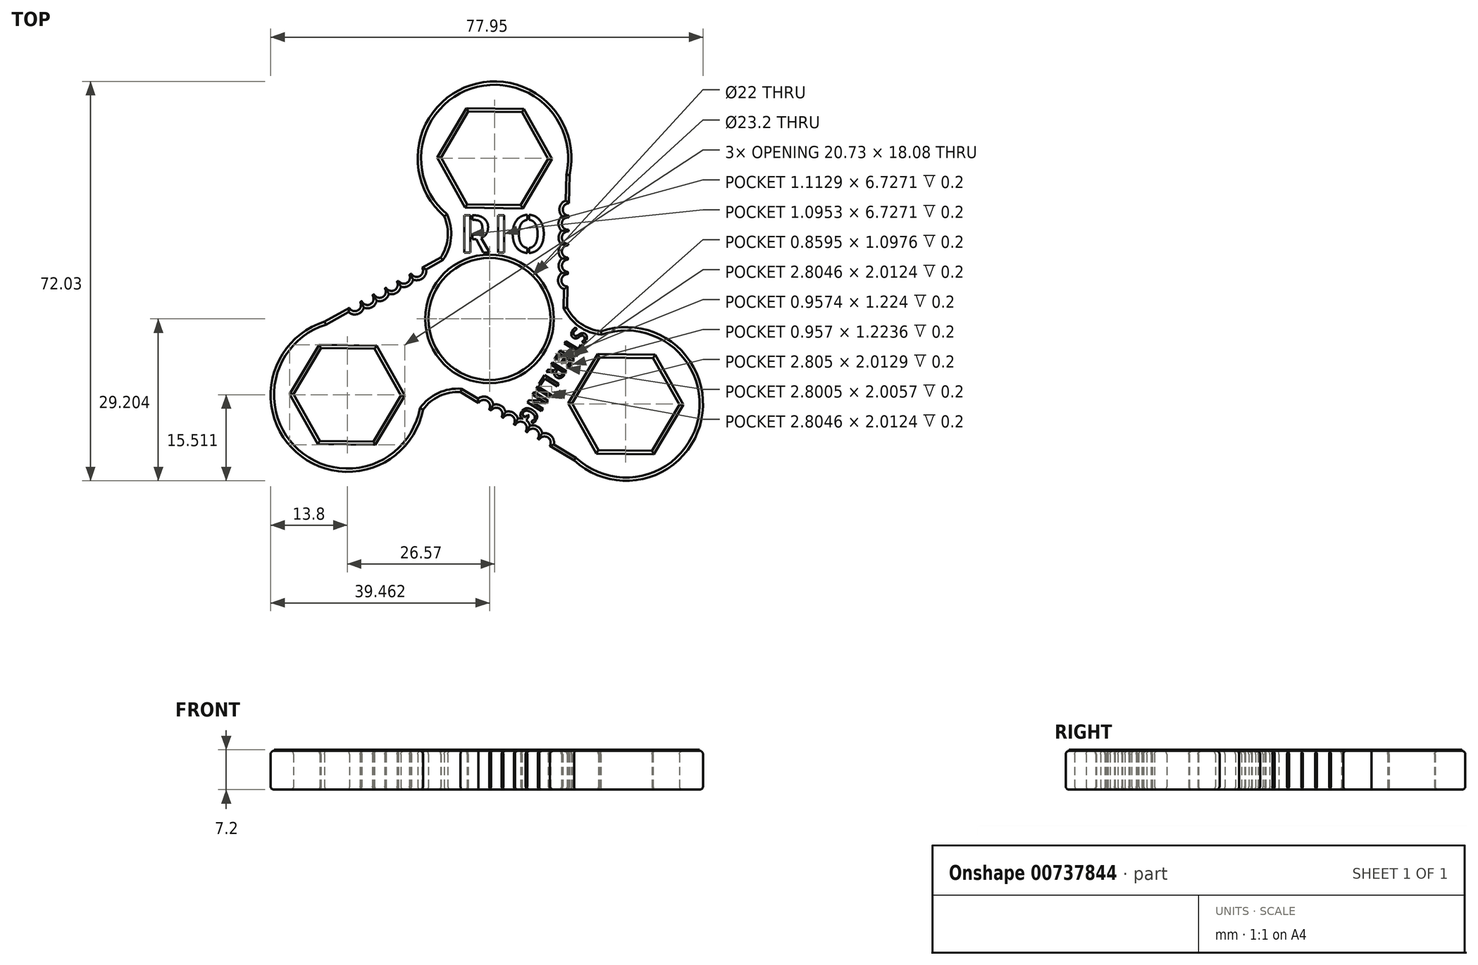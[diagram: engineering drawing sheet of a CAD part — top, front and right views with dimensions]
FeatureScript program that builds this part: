
annotation { "Feature Type Name" : "Feature", "Feature Type Description" : "" }
export const myFeature = defineFeature(function(context is Context, id is Id, definition is map)
    precondition{}
    {
        {
            var Q0;
            Q0=qCreatedBy(makeId("Top.planeOp"),FACE);
            var sketch = newSketch(context, id + "F0", { "sketchPlane" : qUnion([Q0])});
            skCircle(sketch, "E0", {"center": v(0, 0) * mm, "radius": 11 * mm});
            skArc(sketch, "E1", {"start": v(14.5, 25.96) * mm, "mid": v(-3.36, 42.17) * mm, "end": v(-8.1, 18.52) * mm});
            skArc(sketch, "E2", {"start": v(-8.76, 11.09) * mm, "mid": v(-7.48, 14.72) * mm, "end": v(-8.1, 18.52) * mm});
            skLineSegment(sketch, "E3", {"start": v(14.5, 25.96) * mm, "end": v(14.04, 2.08) * mm});
            skCircle(sketch, "E4", {"center": v(14.38, 19.75) * mm, "radius": 1.12 * mm});
            skCircle(sketch, "E5", {"center": v(14.2, 17.22) * mm, "radius": 1.12 * mm});
            skCircle(sketch, "E6", {"center": v(14.22, 14.68) * mm, "radius": 1.12 * mm});
            skCircle(sketch, "E7", {"center": v(14.23, 12.19) * mm, "radius": 1.12 * mm});
            skCircle(sketch, "E8", {"center": v(14.24, 9.62) * mm, "radius": 1.12 * mm});
            skCircle(sketch, "E9", {"center": v(14.14, 6.98) * mm, "radius": 1.12 * mm});
            skArc(sketch, "E10.1.0", {"start": v(-29.67, -0.46) * mm, "mid": v(-34.77, -24.03) * mm, "end": v(-11.93, -16.32) * mm});
            skCircle(sketch, "E10.1.1", {"center": v(0.06, -0.04) * mm, "radius": 11 * mm});
            skLineSegment(sketch, "E10.1.3", {"start": v(-29.67, -0.46) * mm, "end": v(-8.76, 11.09) * mm});
            skArc(sketch, "E10.1.5", {"start": v(-5.16, -13.17) * mm, "mid": v(-8.95, -13.87) * mm, "end": v(-11.93, -16.32) * mm});
            skCircle(sketch, "E10.1.6", {"center": v(-15.39, 7.49) * mm, "radius": 1.12 * mm});
            skCircle(sketch, "E10.1.7", {"center": v(-24.23, 2.54) * mm, "radius": 1.12 * mm});
            skCircle(sketch, "E10.1.8", {"center": v(-21.96, 3.66) * mm, "radius": 1.12 * mm});
            skCircle(sketch, "E10.1.9", {"center": v(-13.05, 8.71) * mm, "radius": 1.12 * mm});
            skCircle(sketch, "E10.1.10", {"center": v(-17.6, 6.2) * mm, "radius": 1.12 * mm});
            skCircle(sketch, "E10.1.11", {"center": v(-19.76, 4.94) * mm, "radius": 1.12 * mm});
            skArc(sketch, "E10.2.0", {"start": v(15.3, -25.5) * mm, "mid": v(38.26, -18.13) * mm, "end": v(20.16, -2.2) * mm});
            skCircle(sketch, "E10.2.1", {"center": v(0.06, 0.03) * mm, "radius": 11 * mm});
            skLineSegment(sketch, "E10.2.3", {"start": v(15.3, -25.5) * mm, "end": v(-5.16, -13.17) * mm});
            skArc(sketch, "E10.2.5", {"start": v(14.04, 2.08) * mm, "mid": v(16.55, -0.85) * mm, "end": v(20.16, -2.2) * mm});
            skCircle(sketch, "E10.2.6", {"center": v(1.27, -17.1) * mm, "radius": 1.12 * mm});
            skCircle(sketch, "E10.2.7", {"center": v(9.98, -22.3) * mm, "radius": 1.12 * mm});
            skCircle(sketch, "E10.2.8", {"center": v(7.87, -20.88) * mm, "radius": 1.12 * mm});
            skCircle(sketch, "E10.2.9", {"center": v(-0.96, -15.7) * mm, "radius": 1.12 * mm});
            skCircle(sketch, "E10.2.10", {"center": v(3.5, -18.38) * mm, "radius": 1.12 * mm});
            skCircle(sketch, "E10.2.11", {"center": v(5.66, -19.62) * mm, "radius": 1.12 * mm});
            skPoint(sketch, "E10.center", {"position": v(0.04, 0) * mm});
            skPoint(sketch, "E11.orphan", {"position": v(14, 0) * mm});
            skPoint(sketch, "E12.orphan", {"position": v(13.84, 2.53) * mm});
            skPoint(sketch, "E13.orphan", {"position": v(-4.67, -13.21) * mm});
            skPoint(sketch, "E14.orphan", {"position": v(-6.94, -12.1) * mm});
            skPoint(sketch, "E15.orphan", {"position": v(-6.94, 12.09) * mm});
            skPoint(sketch, "E16.orphan", {"position": v(-9.05, 10.69) * mm});
            skCircle(sketch, "E17.cCircle", {"center": v(0.97, 29) * mm, "radius": 9.67 * mm, "construction": true});
            skLineSegment(sketch, "E17.0", {"start": v(-3.97, 20.69) * mm, "end": v(-8.7, 29.12) * mm});
            skLineSegment(sketch, "E17.1", {"start": v(-8.7, 29.12) * mm, "end": v(-3.76, 37.43) * mm});
            skLineSegment(sketch, "E17.2", {"start": v(-3.76, 37.43) * mm, "end": v(5.91, 37.31) * mm});
            skLineSegment(sketch, "E17.3", {"start": v(5.91, 37.31) * mm, "end": v(10.64, 28.88) * mm});
            skLineSegment(sketch, "E17.4", {"start": v(10.64, 28.88) * mm, "end": v(5.7, 20.56) * mm});
            skLineSegment(sketch, "E17.5", {"start": v(5.7, 20.56) * mm, "end": v(-3.97, 20.69) * mm});
            skCircle(sketch, "E18.1.0", {"center": v(-25.6, -13.66) * mm, "radius": 9.67 * mm, "construction": true});
            skLineSegment(sketch, "E18.1.1", {"start": v(-20.66, -5.35) * mm, "end": v(-15.93, -13.78) * mm});
            skLineSegment(sketch, "E18.1.2", {"start": v(-15.93, -13.78) * mm, "end": v(-20.87, -22.1) * mm});
            skLineSegment(sketch, "E18.1.3", {"start": v(-20.87, -22.1) * mm, "end": v(-30.54, -21.97) * mm});
            skLineSegment(sketch, "E18.1.4", {"start": v(-30.54, -21.97) * mm, "end": v(-35.27, -13.54) * mm});
            skLineSegment(sketch, "E18.1.5", {"start": v(-35.27, -13.54) * mm, "end": v(-30.33, -5.22) * mm});
            skLineSegment(sketch, "E18.1.6", {"start": v(-30.33, -5.22) * mm, "end": v(-20.66, -5.35) * mm});
            skCircle(sketch, "E18.2.0", {"center": v(24.63, -15.34) * mm, "radius": 9.67 * mm, "construction": true});
            skLineSegment(sketch, "E18.2.1", {"start": v(14.96, -15.22) * mm, "end": v(19.9, -6.9) * mm});
            skLineSegment(sketch, "E18.2.2", {"start": v(19.9, -6.9) * mm, "end": v(29.57, -7.03) * mm});
            skLineSegment(sketch, "E18.2.3", {"start": v(29.57, -7.03) * mm, "end": v(34.3, -15.46) * mm});
            skLineSegment(sketch, "E18.2.4", {"start": v(34.3, -15.46) * mm, "end": v(29.36, -23.78) * mm});
            skLineSegment(sketch, "E18.2.5", {"start": v(29.36, -23.78) * mm, "end": v(19.69, -23.65) * mm});
            skLineSegment(sketch, "E18.2.6", {"start": v(19.69, -23.65) * mm, "end": v(14.96, -15.22) * mm});
            skSolve(sketch);
        }
        {
            var Q0;
            {var subQ13=sQuery(id+"F0.wireOp",EDGE,"E10.2.2");var subQ15=makeQuery(id+"F0.imprint","IMPRINT",VERTEX,{"disambiguationData":[OD(0.0)],"derivedFrom":subQ13});Q0=makeQuery(id+"F0.imprint","IMPRINT",FACE,{"disambiguationData":[TD([[makeQuery(id+"F0.imprint","IMPRINT",EDGE,{"disambiguationData":[TD([[subQ15,-1.0]])],"derivedFrom":subQ13}),-1.0]])]});}
            var Q1;
            {var subQ20=sQuery(id+"F0.wireOp",EDGE,"E10.2.2");var subQ23=makeQuery(id+"F0.imprint","IMPRINT",VERTEX,{"disambiguationData":[OD(1.0)],"derivedFrom":subQ20});Q1=makeQuery(id+"F0.imprint","IMPRINT",FACE,{"disambiguationData":[TD([[makeQuery(id+"F0.imprint","IMPRINT",EDGE,{"disambiguationData":[TD([[subQ23,1.0]])],"derivedFrom":subQ20}),-1.0]])]});}
            var Q2;
            Q2=makeQuery(id+"F0.imprint","IMPRINT",FACE,{"disambiguationData":[TD([[makeQuery(id+"F0.imprint","IMPRINT",EDGE,{"derivedFrom":sQuery(id+"F0.wireOp",EDGE,"5nIq9WOL-Nd7C-9ICE-MlP4-sHmHCP0NrJly")}),-1.0]])]});
            var Q3;
            Q3=makeQuery(id+"F0.imprint","IMPRINT",FACE,{"disambiguationData":[TD([[makeQuery(id+"F0.imprint","IMPRINT",EDGE,{"derivedFrom":sQuery(id+"F0.wireOp",EDGE,"E10.2.1")}),-1.0]])]});
            var Q4;
            {var subQ24=sQuery(id+"F0.wireOp",EDGE,"E10.2.2");var subQ27=makeQuery(id+"F0.imprint","IMPRINT",VERTEX,{"disambiguationData":[OD(2.0)],"derivedFrom":subQ24});Q4=makeQuery(id+"F0.imprint","IMPRINT",FACE,{"disambiguationData":[TD([[makeQuery(id+"F0.imprint","IMPRINT",EDGE,{"disambiguationData":[TD([[subQ27,1.0]])],"derivedFrom":subQ24}),-1.0]])]});}
            var Q5;
            {var subQ0=sQuery(id+"F0.wireOp",EDGE,"E10.2.2");var subQ1=sQuery(id+"F0.wireOp",EDGE,"E3");var subQ2=makeQuery(id+"F0.imprint","INTERSECT",VERTEX,{"derivedFrom":[subQ1,subQ0]});Q5=makeQuery(id+"F0.imprint","IMPRINT",FACE,{"disambiguationData":[TD([[makeQuery(id+"F0.imprint","IMPRINT",EDGE,{"disambiguationData":[TD([[subQ2,1.0]])],"derivedFrom":subQ1}),-1.0]])]});}
            var Q6;
            {var subQ0=sQuery(id+"F0.wireOp",EDGE,"E10.2.3");var subQ1=sQuery(id+"F0.wireOp",EDGE,"E10.2.0");var subQ2=makeQuery(id+"F0.imprint","INTERSECT",VERTEX,{"disambiguationData":[OD(0.0)],"derivedFrom":[subQ1,subQ0]});Q6=makeQuery(id+"F0.imprint","IMPRINT",FACE,{"disambiguationData":[TD([[makeQuery(id+"F0.imprint","IMPRINT",EDGE,{"disambiguationData":[TD([[subQ2,1.0]])],"derivedFrom":subQ1}),1.0]])]});}
            var Q7;
            {var subQ0=sQuery(id+"F0.wireOp",EDGE,"E3");var subQ1=sQuery(id+"F0.wireOp",EDGE,"E1");var subQ2=makeQuery(id+"F0.imprint","INTERSECT",VERTEX,{"disambiguationData":[OD(0.0)],"derivedFrom":[subQ1,subQ0]});Q7=makeQuery(id+"F0.imprint","IMPRINT",FACE,{"disambiguationData":[TD([[makeQuery(id+"F0.imprint","IMPRINT",EDGE,{"disambiguationData":[TD([[subQ2,1.0]])],"derivedFrom":subQ1}),1.0]])]});}
            var Q8;
            {var subQ0=sQuery(id+"F0.wireOp",EDGE,"E10.1.3");var subQ1=sQuery(id+"F0.wireOp",EDGE,"E10.1.0");var subQ2=makeQuery(id+"F0.imprint","INTERSECT",VERTEX,{"disambiguationData":[OD(0.0)],"derivedFrom":[subQ1,subQ0]});Q8=makeQuery(id+"F0.imprint","IMPRINT",FACE,{"disambiguationData":[TD([[makeQuery(id+"F0.imprint","IMPRINT",EDGE,{"disambiguationData":[TD([[subQ2,1.0]])],"derivedFrom":subQ1}),1.0]])]});}
            var Q9;
            {var subQ0=sQuery(id+"F0.wireOp",EDGE,"E10.2.2");var subQ1=sQuery(id+"F0.wireOp",EDGE,"E2");var subQ2=makeQuery(id+"F0.imprint","INTERSECT",VERTEX,{"derivedFrom":[subQ1,subQ0]});Q9=makeQuery(id+"F0.imprint","IMPRINT",FACE,{"disambiguationData":[TD([[makeQuery(id+"F0.imprint","IMPRINT",EDGE,{"disambiguationData":[TD([[subQ2,-1.0]])],"derivedFrom":subQ1}),-1.0]])]});}
            var Q10;
            {var subQ0=sQuery(id+"F0.wireOp",EDGE,"E10.2.2");var subQ1=sQuery(id+"F0.wireOp",EDGE,"E10.1.5");var subQ2=makeQuery(id+"F0.imprint","INTERSECT",VERTEX,{"derivedFrom":[subQ1,subQ0]});Q10=makeQuery(id+"F0.imprint","IMPRINT",FACE,{"disambiguationData":[TD([[makeQuery(id+"F0.imprint","IMPRINT",EDGE,{"disambiguationData":[TD([[subQ2,-1.0]])],"derivedFrom":subQ1}),-1.0]])]});}
            var Q11;
            Q11=makeQuery(id+"F0.imprint","IMPRINT",FACE,{"disambiguationData":[TD([[makeQuery(id+"F0.imprint","IMPRINT",EDGE,{"derivedFrom":sQuery(id+"F0.wireOp",EDGE,"E10.1.4")}),-1.0]])]});
            var Q12;
            Q12=makeQuery(id+"F0.imprint","IMPRINT",FACE,{"disambiguationData":[TD([[makeQuery(id+"F0.imprint","IMPRINT",EDGE,{"derivedFrom":sQuery(id+"F0.wireOp",EDGE,"E10.2.4")}),-1.0]])]});
            var Q13;
            {var subQ0=sQuery(id+"F0.wireOp",EDGE,"E10.2.2");var subQ1=sQuery(id+"F0.wireOp",EDGE,"E1");var subQ2=makeQuery(id+"F0.imprint","INTERSECT",VERTEX,{"disambiguationData":[OD(0.0)],"derivedFrom":[subQ1,subQ0]});Q13=makeQuery(id+"F0.imprint","IMPRINT",FACE,{"disambiguationData":[TD([[makeQuery(id+"F0.imprint","IMPRINT",EDGE,{"disambiguationData":[TD([[subQ2,-1.0]])],"derivedFrom":subQ1}),1.0]])]});}
            var Q14;
            {var subQ0=sQuery(id+"F0.wireOp",EDGE,"E10.2.2");var subQ1=sQuery(id+"F0.wireOp",EDGE,"E10.2.0");var subQ2=makeQuery(id+"F0.imprint","INTERSECT",VERTEX,{"disambiguationData":[OD(0.0)],"derivedFrom":[subQ1,subQ0]});Q14=makeQuery(id+"F0.imprint","IMPRINT",FACE,{"disambiguationData":[TD([[makeQuery(id+"F0.imprint","IMPRINT",EDGE,{"disambiguationData":[TD([[subQ2,-1.0]])],"derivedFrom":subQ1}),1.0]])]});}
            var Q15;
            {var subQ0=sQuery(id+"F0.wireOp",EDGE,"E10.2.2");var subQ1=sQuery(id+"F0.wireOp",EDGE,"E10.1.0");var subQ2=makeQuery(id+"F0.imprint","INTERSECT",VERTEX,{"disambiguationData":[OD(0.0)],"derivedFrom":[subQ1,subQ0]});Q15=makeQuery(id+"F0.imprint","IMPRINT",FACE,{"disambiguationData":[TD([[makeQuery(id+"F0.imprint","IMPRINT",EDGE,{"disambiguationData":[TD([[subQ2,-1.0]])],"derivedFrom":subQ1}),1.0]])]});}
            extrude(context, id + "F1", {"entities" : qUnion([Q0, Q1, Q2, Q3, Q4, Q5, Q6, Q7, Q8, Q9, Q10, Q11, Q12, Q13, Q14, Q15]), "depth" : 7 * mm, "offsetDistance" : 25 * mm});
        }
        {
            var Q0;
            Q0=makeQuery(id+"F1.opExtrude","CAP_EDGE",EDGE,{"disambiguationData":[OSD([sQuery(id+"F0.wireOp",EDGE,"E10.1.5")])],"isStart":false});
            var Q1;
            {var subQ0=sQuery(id+"F0.wireOp",EDGE,"E10.2.3");Q1=makeQuery(id+"F1.opExtrude","CAP_EDGE",EDGE,{"disambiguationData":[OSD([subQ0]),TDD([makeQuery(id+"F0.imprint","IMPRINT",EDGE,{"disambiguationData":[TD([[makeQuery(id+"F0.imprint","INTERSECT",VERTEX,{"derivedFrom":[sQuery(id+"F0.wireOp",EDGE,"E10.1.5"),subQ0]}),1.0]])],"derivedFrom":subQ0})])],"isStart":false});}
            var Q2;
            Q2=makeQuery(id+"F1.opExtrude","CAP_EDGE",EDGE,{"disambiguationData":[OSD([sQuery(id+"F0.wireOp",EDGE,"E10.1.0")])],"isStart":false});
            var Q3;
            Q3=makeQuery(id+"F1.opExtrude","CAP_EDGE",EDGE,{"disambiguationData":[OSD([sQuery(id+"F0.wireOp",EDGE,"E10.1.0")])],"isStart":true});
            var Q4;
            {var subQ0=sQuery(id+"F0.wireOp",EDGE,"E10.1.3");Q4=makeQuery(id+"F1.opExtrude","CAP_EDGE",EDGE,{"disambiguationData":[OSD([subQ0]),TDD([makeQuery(id+"F0.imprint","IMPRINT",EDGE,{"disambiguationData":[TD([[makeQuery(id+"F0.imprint","INTERSECT",VERTEX,{"disambiguationData":[OD(1.0)],"derivedFrom":[sQuery(id+"F0.wireOp",EDGE,"E10.1.0"),subQ0]}),-1.0]])],"derivedFrom":subQ0})])],"isStart":true});}
            var Q5;
            {var subQ0=sQuery(id+"F0.wireOp",EDGE,"E10.1.3");Q5=makeQuery(id+"F1.opExtrude","CAP_EDGE",EDGE,{"disambiguationData":[OSD([subQ0]),TDD([makeQuery(id+"F0.imprint","IMPRINT",EDGE,{"disambiguationData":[TD([[makeQuery(id+"F0.imprint","INTERSECT",VERTEX,{"disambiguationData":[OD(1.0)],"derivedFrom":[sQuery(id+"F0.wireOp",EDGE,"E10.1.0"),subQ0]}),-1.0]])],"derivedFrom":subQ0})])],"isStart":false});}
            var Q6;
            Q6=makeQuery(id+"F1.opExtrude","CAP_EDGE",EDGE,{"disambiguationData":[OSD([sQuery(id+"F0.wireOp",EDGE,"E10.1.5")])],"isStart":true});
            var Q7;
            {var subQ0=sQuery(id+"F0.wireOp",EDGE,"E10.2.3");Q7=makeQuery(id+"F1.opExtrude","CAP_EDGE",EDGE,{"disambiguationData":[OSD([subQ0]),TDD([makeQuery(id+"F0.imprint","IMPRINT",EDGE,{"disambiguationData":[TD([[makeQuery(id+"F0.imprint","INTERSECT",VERTEX,{"derivedFrom":[sQuery(id+"F0.wireOp",EDGE,"E10.1.5"),subQ0]}),1.0]])],"derivedFrom":subQ0})])],"isStart":true});}
            var Q8;
            Q8=makeQuery(id+"F1.opExtrude","CAP_EDGE",EDGE,{"disambiguationData":[OSD([sQuery(id+"F0.wireOp",EDGE,"E10.1.4")])],"isStart":false});
            var Q9;
            Q9=makeQuery(id+"F1.opExtrude","CAP_EDGE",EDGE,{"disambiguationData":[OSD([sQuery(id+"F0.wireOp",EDGE,"E10.1.4")])],"isStart":true});
            var Q10;
            Q10=makeQuery(id+"F1.opExtrude","CAP_EDGE",EDGE,{"disambiguationData":[OSD([sQuery(id+"F0.wireOp",EDGE,"E10.2.1")])],"isStart":true});
            var Q11;
            Q11=makeQuery(id+"F1.opExtrude","CAP_EDGE",EDGE,{"disambiguationData":[OSD([sQuery(id+"F0.wireOp",EDGE,"E10.2.1")])],"isStart":false});
            var Q12;
            {var subQ0=sQuery(id+"F0.wireOp",EDGE,"E10.1.3");Q12=makeQuery(id+"F1.opExtrude","CAP_EDGE",EDGE,{"disambiguationData":[OSD([subQ0]),TDD([makeQuery(id+"F0.imprint","IMPRINT",EDGE,{"disambiguationData":[TD([[makeQuery(id+"F0.imprint","INTERSECT",VERTEX,{"derivedFrom":[sQuery(id+"F0.wireOp",EDGE,"E2"),subQ0]}),1.0]])],"derivedFrom":subQ0})])],"isStart":false});}
            var Q13;
            Q13=makeQuery(id+"F1.opExtrude","CAP_EDGE",EDGE,{"disambiguationData":[OSD([sQuery(id+"F0.wireOp",EDGE,"E2")])],"isStart":false});
            var Q14;
            Q14=makeQuery(id+"F1.opExtrude","CAP_EDGE",EDGE,{"disambiguationData":[OSD([sQuery(id+"F0.wireOp",EDGE,"E1")])],"isStart":false});
            var Q15;
            Q15=makeQuery(id+"F1.opExtrude","CAP_EDGE",EDGE,{"disambiguationData":[OSD([sQuery(id+"F0.wireOp",EDGE,"5nIq9WOL-Nd7C-9ICE-MlP4-sHmHCP0NrJly")])],"isStart":false});
            var Q16;
            Q16=makeQuery(id+"F1.opExtrude","CAP_EDGE",EDGE,{"disambiguationData":[OSD([sQuery(id+"F0.wireOp",EDGE,"5nIq9WOL-Nd7C-9ICE-MlP4-sHmHCP0NrJly")])],"isStart":true});
            var Q17;
            Q17=makeQuery(id+"F1.opExtrude","CAP_EDGE",EDGE,{"disambiguationData":[OSD([sQuery(id+"F0.wireOp",EDGE,"E1")])],"isStart":true});
            var Q18;
            Q18=makeQuery(id+"F1.opExtrude","CAP_EDGE",EDGE,{"disambiguationData":[OSD([sQuery(id+"F0.wireOp",EDGE,"E2")])],"isStart":true});
            var Q19;
            {var subQ0=sQuery(id+"F0.wireOp",EDGE,"E10.1.3");Q19=makeQuery(id+"F1.opExtrude","CAP_EDGE",EDGE,{"disambiguationData":[OSD([subQ0]),TDD([makeQuery(id+"F0.imprint","IMPRINT",EDGE,{"disambiguationData":[TD([[makeQuery(id+"F0.imprint","INTERSECT",VERTEX,{"derivedFrom":[sQuery(id+"F0.wireOp",EDGE,"E2"),subQ0]}),1.0]])],"derivedFrom":subQ0})])],"isStart":true});}
            var Q20;
            Q20=makeQuery(id+"F1.opExtrude","CAP_EDGE",EDGE,{"disambiguationData":[OSD([sQuery(id+"F0.wireOp",EDGE,"E10.2.5")])],"isStart":false});
            var Q21;
            {var subQ0=sQuery(id+"F0.wireOp",EDGE,"E3");Q21=makeQuery(id+"F1.opExtrude","CAP_EDGE",EDGE,{"disambiguationData":[OSD([subQ0]),TDD([makeQuery(id+"F0.imprint","IMPRINT",EDGE,{"disambiguationData":[TD([[makeQuery(id+"F0.imprint","INTERSECT",VERTEX,{"disambiguationData":[OD(1.0)],"derivedFrom":[subQ0,sQuery(id+"F0.wireOp",EDGE,"E9")]}),-1.0]])],"derivedFrom":subQ0})])],"isStart":false});}
            var Q22;
            Q22=makeQuery(id+"F1.opExtrude","CAP_EDGE",EDGE,{"disambiguationData":[OSD([sQuery(id+"F0.wireOp",EDGE,"E10.2.0")])],"isStart":false});
            var Q23;
            Q23=makeQuery(id+"F1.opExtrude","CAP_EDGE",EDGE,{"disambiguationData":[OSD([sQuery(id+"F0.wireOp",EDGE,"E10.2.4")])],"isStart":false});
            var Q24;
            Q24=makeQuery(id+"F1.opExtrude","CAP_EDGE",EDGE,{"disambiguationData":[OSD([sQuery(id+"F0.wireOp",EDGE,"E10.2.4")])],"isStart":true});
            var Q25;
            Q25=makeQuery(id+"F1.opExtrude","CAP_EDGE",EDGE,{"disambiguationData":[OSD([sQuery(id+"F0.wireOp",EDGE,"E10.2.5")])],"isStart":true});
            var Q26;
            Q26=makeQuery(id+"F1.opExtrude","CAP_EDGE",EDGE,{"disambiguationData":[OSD([sQuery(id+"F0.wireOp",EDGE,"E10.2.0")])],"isStart":true});
            var Q27;
            Q27=makeQuery(id+"F1.opExtrude","CAP_EDGE",EDGE,{"disambiguationData":[OSD([sQuery(id+"F0.wireOp",EDGE,"E10.1.7")])],"isStart":false});
            var Q28;
            Q28=makeQuery(id+"F1.opExtrude","CAP_FACE",FACE,{"disambiguationData":[OSD([sQuery(id+"F0.wireOp",EDGE,"5nIq9WOL-Nd7C-9ICE-MlP4-sHmHCP0NrJly"),sQuery(id+"F0.wireOp",EDGE,"E1"),sQuery(id+"F0.wireOp",EDGE,"E2"),sQuery(id+"F0.wireOp",EDGE,"E3"),sQuery(id+"F0.wireOp",EDGE,"E4"),sQuery(id+"F0.wireOp",EDGE,"E5"),sQuery(id+"F0.wireOp",EDGE,"E6"),sQuery(id+"F0.wireOp",EDGE,"E7"),sQuery(id+"F0.wireOp",EDGE,"E8"),sQuery(id+"F0.wireOp",EDGE,"E9"),sQuery(id+"F0.wireOp",EDGE,"E10.1.0"),sQuery(id+"F0.wireOp",EDGE,"E10.1.3"),sQuery(id+"F0.wireOp",EDGE,"E10.1.4"),sQuery(id+"F0.wireOp",EDGE,"E10.1.5"),sQuery(id+"F0.wireOp",EDGE,"E10.1.6"),sQuery(id+"F0.wireOp",EDGE,"E10.1.7"),sQuery(id+"F0.wireOp",EDGE,"E10.1.8"),sQuery(id+"F0.wireOp",EDGE,"E10.1.9"),sQuery(id+"F0.wireOp",EDGE,"E10.1.10"),sQuery(id+"F0.wireOp",EDGE,"E10.1.11"),sQuery(id+"F0.wireOp",EDGE,"E10.2.0"),sQuery(id+"F0.wireOp",EDGE,"E10.2.1"),sQuery(id+"F0.wireOp",EDGE,"E10.2.3"),sQuery(id+"F0.wireOp",EDGE,"E10.2.4"),sQuery(id+"F0.wireOp",EDGE,"E10.2.5"),sQuery(id+"F0.wireOp",EDGE,"E10.2.6"),sQuery(id+"F0.wireOp",EDGE,"E10.2.7"),sQuery(id+"F0.wireOp",EDGE,"E10.2.8"),sQuery(id+"F0.wireOp",EDGE,"E10.2.9"),sQuery(id+"F0.wireOp",EDGE,"E10.2.10"),sQuery(id+"F0.wireOp",EDGE,"E10.2.11")])],"isStart":false});
            var Q29;
            Q29=makeQuery(id+"F1.opExtrude","CAP_EDGE",EDGE,{"disambiguationData":[OSD([sQuery(id+"F0.wireOp",EDGE,"E10.1.8")])],"isStart":false});
            var Q30;
            Q30=makeQuery(id+"F1.opExtrude","CAP_EDGE",EDGE,{"disambiguationData":[OSD([sQuery(id+"F0.wireOp",EDGE,"E10.1.11")])],"isStart":false});
            var Q31;
            Q31=makeQuery(id+"F1.opExtrude","CAP_EDGE",EDGE,{"disambiguationData":[OSD([sQuery(id+"F0.wireOp",EDGE,"E10.1.7")])],"isStart":true});
            var Q32;
            Q32=makeQuery(id+"F1.opExtrude","CAP_EDGE",EDGE,{"disambiguationData":[OSD([sQuery(id+"F0.wireOp",EDGE,"E10.1.8")])],"isStart":true});
            var Q33;
            Q33=makeQuery(id+"F1.opExtrude","CAP_EDGE",EDGE,{"disambiguationData":[OSD([sQuery(id+"F0.wireOp",EDGE,"E10.1.11")])],"isStart":true});
            var Q34;
            Q34=makeQuery(id+"F1.opExtrude","CAP_EDGE",EDGE,{"disambiguationData":[OSD([sQuery(id+"F0.wireOp",EDGE,"E10.1.10")])],"isStart":true});
            var Q35;
            Q35=makeQuery(id+"F1.opExtrude","CAP_EDGE",EDGE,{"disambiguationData":[OSD([sQuery(id+"F0.wireOp",EDGE,"E10.1.9")])],"isStart":true});
            var Q36;
            Q36=makeQuery(id+"F1.opExtrude","CAP_FACE",FACE,{"disambiguationData":[OSD([sQuery(id+"F0.wireOp",EDGE,"5nIq9WOL-Nd7C-9ICE-MlP4-sHmHCP0NrJly"),sQuery(id+"F0.wireOp",EDGE,"E1"),sQuery(id+"F0.wireOp",EDGE,"E2"),sQuery(id+"F0.wireOp",EDGE,"E3"),sQuery(id+"F0.wireOp",EDGE,"E4"),sQuery(id+"F0.wireOp",EDGE,"E5"),sQuery(id+"F0.wireOp",EDGE,"E6"),sQuery(id+"F0.wireOp",EDGE,"E7"),sQuery(id+"F0.wireOp",EDGE,"E8"),sQuery(id+"F0.wireOp",EDGE,"E9"),sQuery(id+"F0.wireOp",EDGE,"E10.1.0"),sQuery(id+"F0.wireOp",EDGE,"E10.1.3"),sQuery(id+"F0.wireOp",EDGE,"E10.1.4"),sQuery(id+"F0.wireOp",EDGE,"E10.1.5"),sQuery(id+"F0.wireOp",EDGE,"E10.1.6"),sQuery(id+"F0.wireOp",EDGE,"E10.1.7"),sQuery(id+"F0.wireOp",EDGE,"E10.1.8"),sQuery(id+"F0.wireOp",EDGE,"E10.1.9"),sQuery(id+"F0.wireOp",EDGE,"E10.1.10"),sQuery(id+"F0.wireOp",EDGE,"E10.1.11"),sQuery(id+"F0.wireOp",EDGE,"E10.2.0"),sQuery(id+"F0.wireOp",EDGE,"E10.2.1"),sQuery(id+"F0.wireOp",EDGE,"E10.2.3"),sQuery(id+"F0.wireOp",EDGE,"E10.2.4"),sQuery(id+"F0.wireOp",EDGE,"E10.2.5"),sQuery(id+"F0.wireOp",EDGE,"E10.2.6"),sQuery(id+"F0.wireOp",EDGE,"E10.2.7"),sQuery(id+"F0.wireOp",EDGE,"E10.2.8"),sQuery(id+"F0.wireOp",EDGE,"E10.2.9"),sQuery(id+"F0.wireOp",EDGE,"E10.2.10"),sQuery(id+"F0.wireOp",EDGE,"E10.2.11")])],"isStart":true});
            var Q37;
            Q37=makeQuery(id+"F1.opExtrude","CAP_EDGE",EDGE,{"disambiguationData":[OSD([sQuery(id+"F0.wireOp",EDGE,"E10.1.6")])],"isStart":true});
            fillet(context, id + "F2", {"entities" : qUnion([Q0, Q1, Q2, Q3, Q4, Q5, Q6, Q7, Q8, Q9, Q10, Q11, Q12, Q13, Q14, Q15, Q16, Q17, Q18, Q19, Q20, Q21, Q22, Q23, Q24, Q25, Q26, Q27, Q28, Q29, Q30, Q31, Q32, Q33, Q34, Q35, Q36, Q37]), "radius" : 0.6 * mm, "tangentPropagation" : true, "allowEdgeOverflow" : false});
        }
        {
            var Q0;
            Q0=makeQuery(id+"F1.opExtrude","CAP_FACE",FACE,{"disambiguationData":[OSD([sQuery(id+"F0.wireOp",EDGE,"5nIq9WOL-Nd7C-9ICE-MlP4-sHmHCP0NrJly"),sQuery(id+"F0.wireOp",EDGE,"E1"),sQuery(id+"F0.wireOp",EDGE,"E2"),sQuery(id+"F0.wireOp",EDGE,"E3"),sQuery(id+"F0.wireOp",EDGE,"E4"),sQuery(id+"F0.wireOp",EDGE,"E5"),sQuery(id+"F0.wireOp",EDGE,"E6"),sQuery(id+"F0.wireOp",EDGE,"E7"),sQuery(id+"F0.wireOp",EDGE,"E8"),sQuery(id+"F0.wireOp",EDGE,"E9"),sQuery(id+"F0.wireOp",EDGE,"E10.1.0"),sQuery(id+"F0.wireOp",EDGE,"E10.1.3"),sQuery(id+"F0.wireOp",EDGE,"E10.1.4"),sQuery(id+"F0.wireOp",EDGE,"E10.1.5"),sQuery(id+"F0.wireOp",EDGE,"E10.1.6"),sQuery(id+"F0.wireOp",EDGE,"E10.1.7"),sQuery(id+"F0.wireOp",EDGE,"E10.1.8"),sQuery(id+"F0.wireOp",EDGE,"E10.1.9"),sQuery(id+"F0.wireOp",EDGE,"E10.1.10"),sQuery(id+"F0.wireOp",EDGE,"E10.1.11"),sQuery(id+"F0.wireOp",EDGE,"E10.2.0"),sQuery(id+"F0.wireOp",EDGE,"E10.2.1"),sQuery(id+"F0.wireOp",EDGE,"E10.2.3"),sQuery(id+"F0.wireOp",EDGE,"E10.2.4"),sQuery(id+"F0.wireOp",EDGE,"E10.2.5"),sQuery(id+"F0.wireOp",EDGE,"E10.2.6"),sQuery(id+"F0.wireOp",EDGE,"E10.2.7"),sQuery(id+"F0.wireOp",EDGE,"E10.2.8"),sQuery(id+"F0.wireOp",EDGE,"E10.2.9"),sQuery(id+"F0.wireOp",EDGE,"E10.2.10"),sQuery(id+"F0.wireOp",EDGE,"E10.2.11")])],"isStart":false});
            var sketch = newSketch(context, id + "F3", { "sketchPlane" : qUnion([Q0])});
            skSolve(sketch);
        }
        {
            var Q0;
            {var subQ0=sQuery(id+"F0.wireOp",EDGE,"E18.2.6");var subQ1=sQuery(id+"F0.wireOp",EDGE,"E18.2.5");var subQ2=sQuery(id+"F0.wireOp",EDGE,"E18.2.4");var subQ3=sQuery(id+"F0.wireOp",EDGE,"E18.2.3");var subQ4=sQuery(id+"F0.wireOp",EDGE,"E18.2.2");var subQ5=sQuery(id+"F0.wireOp",EDGE,"E18.2.1");var subQ6=sQuery(id+"F0.wireOp",EDGE,"E18.1.6");var subQ7=sQuery(id+"F0.wireOp",EDGE,"E18.1.5");var subQ8=sQuery(id+"F0.wireOp",EDGE,"E18.1.4");var subQ9=sQuery(id+"F0.wireOp",EDGE,"E18.1.3");var subQ10=sQuery(id+"F0.wireOp",EDGE,"E18.1.2");var subQ11=sQuery(id+"F0.wireOp",EDGE,"E18.1.1");var subQ12=sQuery(id+"F0.wireOp",EDGE,"E17.5");var subQ13=sQuery(id+"F0.wireOp",EDGE,"E17.4");var subQ14=sQuery(id+"F0.wireOp",EDGE,"E17.3");var subQ15=sQuery(id+"F0.wireOp",EDGE,"E17.2");var subQ16=sQuery(id+"F0.wireOp",EDGE,"E17.1");var subQ17=sQuery(id+"F0.wireOp",EDGE,"E17.0");var subQ18=sQuery(id+"F0.wireOp",EDGE,"E10.2.11");var subQ19=sQuery(id+"F0.wireOp",EDGE,"E10.2.10");var subQ20=sQuery(id+"F0.wireOp",EDGE,"E10.2.9");var subQ21=sQuery(id+"F0.wireOp",EDGE,"E10.2.8");var subQ22=sQuery(id+"F0.wireOp",EDGE,"E10.2.7");var subQ23=sQuery(id+"F0.wireOp",EDGE,"E10.2.6");var subQ24=sQuery(id+"F0.wireOp",EDGE,"E10.2.5");var subQ25=sQuery(id+"F0.wireOp",EDGE,"E10.2.3");var subQ26=sQuery(id+"F0.wireOp",EDGE,"E10.2.1");var subQ27=sQuery(id+"F0.wireOp",EDGE,"E10.2.0");var subQ28=sQuery(id+"F0.wireOp",EDGE,"E10.1.11");var subQ29=sQuery(id+"F0.wireOp",EDGE,"E10.1.10");var subQ30=sQuery(id+"F0.wireOp",EDGE,"E10.1.9");var subQ31=sQuery(id+"F0.wireOp",EDGE,"E10.1.8");var subQ32=sQuery(id+"F0.wireOp",EDGE,"E10.1.7");var subQ33=sQuery(id+"F0.wireOp",EDGE,"E10.1.6");var subQ34=sQuery(id+"F0.wireOp",EDGE,"E10.1.5");var subQ35=sQuery(id+"F0.wireOp",EDGE,"E10.1.3");var subQ36=sQuery(id+"F0.wireOp",EDGE,"E10.1.0");var subQ37=sQuery(id+"F0.wireOp",EDGE,"E9");var subQ38=sQuery(id+"F0.wireOp",EDGE,"E8");var subQ39=sQuery(id+"F0.wireOp",EDGE,"E7");var subQ40=sQuery(id+"F0.wireOp",EDGE,"E6");var subQ41=sQuery(id+"F0.wireOp",EDGE,"E5");var subQ42=sQuery(id+"F0.wireOp",EDGE,"E4");var subQ43=sQuery(id+"F0.wireOp",EDGE,"E3");var subQ44=sQuery(id+"F0.wireOp",EDGE,"E2");var subQ45=sQuery(id+"F0.wireOp",EDGE,"E1");var subQ46=makeQuery(id+"F1.opExtrude","CAP_FACE",FACE,{"disambiguationData":[OSD([subQ45,subQ44,subQ43,subQ42,subQ41,subQ40,subQ39,subQ38,subQ37,subQ36,subQ35,subQ34,subQ33,subQ32,subQ31,subQ30,subQ29,subQ28,subQ27,subQ26,subQ25,subQ24,subQ23,subQ22,subQ21,subQ20,subQ19,subQ18,subQ17,subQ16,subQ15,subQ14,subQ13,subQ12,subQ11,subQ10,subQ9,subQ8,subQ7,subQ6,subQ5,subQ4,subQ3,subQ2,subQ1,subQ0])],"isStart":false});Q0=makeQuery(id+"F3.imprint","IMPRINT",FACE,{"disambiguationData":[TD([[makeQuery(id+"F3.imprint","IMPRINT",EDGE,{"derivedFrom":makeQuery(id+"F2.opFillet","BLEND_EDGE",EDGE,{"blendedFrom":[makeQuery(id+"F1.opExtrude","CAP_EDGE",EDGE,{"disambiguationData":[OSD([subQ45])],"isStart":false}),subQ46],"blendedInto":[subQ46]})}),1.0]])]});}
            var sketch = newSketch(context, id + "F4", { "sketchPlane" : qUnion([Q0])});
            skText(sketch, "E19", { "text": "RIO", "fontName": "AllertaStencil-Regular.ttf"});
            const initialGuessF4  = {"E19": [-0.0053, 0.01197, 1, 0, 0.00673]};
            skSetInitialGuess(sketch, initialGuessF4);
            skSolve(sketch);
        }
        {
            var Q0;
            {var subQ0=sQuery(id+"F0.wireOp",EDGE,"E18.2.6");var subQ1=sQuery(id+"F0.wireOp",EDGE,"E18.2.5");var subQ2=sQuery(id+"F0.wireOp",EDGE,"E18.2.4");var subQ3=sQuery(id+"F0.wireOp",EDGE,"E18.2.3");var subQ4=sQuery(id+"F0.wireOp",EDGE,"E18.2.2");var subQ5=sQuery(id+"F0.wireOp",EDGE,"E18.2.1");var subQ6=sQuery(id+"F0.wireOp",EDGE,"E18.1.6");var subQ7=sQuery(id+"F0.wireOp",EDGE,"E18.1.5");var subQ8=sQuery(id+"F0.wireOp",EDGE,"E18.1.4");var subQ9=sQuery(id+"F0.wireOp",EDGE,"E18.1.3");var subQ10=sQuery(id+"F0.wireOp",EDGE,"E18.1.2");var subQ11=sQuery(id+"F0.wireOp",EDGE,"E18.1.1");var subQ12=sQuery(id+"F0.wireOp",EDGE,"E17.5");var subQ13=sQuery(id+"F0.wireOp",EDGE,"E17.4");var subQ14=sQuery(id+"F0.wireOp",EDGE,"E17.3");var subQ15=sQuery(id+"F0.wireOp",EDGE,"E17.2");var subQ16=sQuery(id+"F0.wireOp",EDGE,"E17.1");var subQ17=sQuery(id+"F0.wireOp",EDGE,"E17.0");var subQ18=sQuery(id+"F0.wireOp",EDGE,"E10.2.11");var subQ19=sQuery(id+"F0.wireOp",EDGE,"E10.2.10");var subQ20=sQuery(id+"F0.wireOp",EDGE,"E10.2.9");var subQ21=sQuery(id+"F0.wireOp",EDGE,"E10.2.8");var subQ22=sQuery(id+"F0.wireOp",EDGE,"E10.2.7");var subQ23=sQuery(id+"F0.wireOp",EDGE,"E10.2.6");var subQ24=sQuery(id+"F0.wireOp",EDGE,"E10.2.5");var subQ25=sQuery(id+"F0.wireOp",EDGE,"E10.2.3");var subQ26=sQuery(id+"F0.wireOp",EDGE,"E10.2.1");var subQ27=sQuery(id+"F0.wireOp",EDGE,"E10.2.0");var subQ28=sQuery(id+"F0.wireOp",EDGE,"E10.1.11");var subQ29=sQuery(id+"F0.wireOp",EDGE,"E10.1.10");var subQ30=sQuery(id+"F0.wireOp",EDGE,"E10.1.9");var subQ31=sQuery(id+"F0.wireOp",EDGE,"E10.1.8");var subQ32=sQuery(id+"F0.wireOp",EDGE,"E10.1.7");var subQ33=sQuery(id+"F0.wireOp",EDGE,"E10.1.6");var subQ34=sQuery(id+"F0.wireOp",EDGE,"E10.1.5");var subQ35=sQuery(id+"F0.wireOp",EDGE,"E10.1.3");var subQ36=sQuery(id+"F0.wireOp",EDGE,"E10.1.0");var subQ37=sQuery(id+"F0.wireOp",EDGE,"E9");var subQ38=sQuery(id+"F0.wireOp",EDGE,"E8");var subQ39=sQuery(id+"F0.wireOp",EDGE,"E7");var subQ40=sQuery(id+"F0.wireOp",EDGE,"E6");var subQ41=sQuery(id+"F0.wireOp",EDGE,"E5");var subQ42=sQuery(id+"F0.wireOp",EDGE,"E4");var subQ43=sQuery(id+"F0.wireOp",EDGE,"E3");var subQ44=sQuery(id+"F0.wireOp",EDGE,"E2");var subQ45=sQuery(id+"F0.wireOp",EDGE,"E1");var subQ46=makeQuery(id+"F1.opExtrude","CAP_FACE",FACE,{"disambiguationData":[OSD([subQ45,subQ44,subQ43,subQ42,subQ41,subQ40,subQ39,subQ38,subQ37,subQ36,subQ35,subQ34,subQ33,subQ32,subQ31,subQ30,subQ29,subQ28,subQ27,subQ26,subQ25,subQ24,subQ23,subQ22,subQ21,subQ20,subQ19,subQ18,subQ17,subQ16,subQ15,subQ14,subQ13,subQ12,subQ11,subQ10,subQ9,subQ8,subQ7,subQ6,subQ5,subQ4,subQ3,subQ2,subQ1,subQ0])],"isStart":false});Q0=makeQuery(id+"F3.imprint","IMPRINT",FACE,{"disambiguationData":[TD([[makeQuery(id+"F3.imprint","IMPRINT",EDGE,{"derivedFrom":makeQuery(id+"F2.opFillet","BLEND_EDGE",EDGE,{"blendedFrom":[makeQuery(id+"F1.opExtrude","CAP_EDGE",EDGE,{"disambiguationData":[OSD([subQ45])],"isStart":false}),subQ46],"blendedInto":[subQ46]})}),1.0]])]});}
            var Q1;
            Q1 = qSketchRegion(id + "F4", true);
            extrude(context, id + "F5", {"entities" : qUnion([Q0, Q1]), "operationType" : NewBodyOperationType.ADD, "depth" : 0.2 * mm, "offsetDistance" : 25 * mm});
        }
        {
            var Q0;
            Q0 = qSketchRegion(id + "F4", true);
            extrude(context, id + "F6", {"entities" : qUnion([Q0]), "depth" : 0.2 * mm, "offsetDistance" : 25 * mm});
        }
        {
            var Q0;
            Q0 = qSketchRegion(id + "F4", true);
            extrude(context, id + "F7", {"entities" : qUnion([Q0]), "operationType" : NewBodyOperationType.REMOVE, "depth" : 0.2 * mm, "offsetDistance" : 25 * mm});
        }
        {
            var Q0;
            Q0=makeQuery(id+"F5.opExtrude","CAP_FACE",FACE,{"disambiguationData":[OSD([sQuery(id+"F0.wireOp",EDGE,"E1"),sQuery(id+"F0.wireOp",EDGE,"E2"),sQuery(id+"F0.wireOp",EDGE,"E3"),sQuery(id+"F0.wireOp",EDGE,"E4"),sQuery(id+"F0.wireOp",EDGE,"E5"),sQuery(id+"F0.wireOp",EDGE,"E6"),sQuery(id+"F0.wireOp",EDGE,"E7"),sQuery(id+"F0.wireOp",EDGE,"E8"),sQuery(id+"F0.wireOp",EDGE,"E9"),sQuery(id+"F0.wireOp",EDGE,"E10.1.0"),sQuery(id+"F0.wireOp",EDGE,"E10.1.3"),sQuery(id+"F0.wireOp",EDGE,"E10.1.5"),sQuery(id+"F0.wireOp",EDGE,"E10.1.6"),sQuery(id+"F0.wireOp",EDGE,"E10.1.7"),sQuery(id+"F0.wireOp",EDGE,"E10.1.8"),sQuery(id+"F0.wireOp",EDGE,"E10.1.9"),sQuery(id+"F0.wireOp",EDGE,"E10.1.10"),sQuery(id+"F0.wireOp",EDGE,"E10.1.11"),sQuery(id+"F0.wireOp",EDGE,"E10.2.0"),sQuery(id+"F0.wireOp",EDGE,"E10.2.1"),sQuery(id+"F0.wireOp",EDGE,"E10.2.3"),sQuery(id+"F0.wireOp",EDGE,"E10.2.5"),sQuery(id+"F0.wireOp",EDGE,"E10.2.6"),sQuery(id+"F0.wireOp",EDGE,"E10.2.7"),sQuery(id+"F0.wireOp",EDGE,"E10.2.8"),sQuery(id+"F0.wireOp",EDGE,"E10.2.9"),sQuery(id+"F0.wireOp",EDGE,"E10.2.10"),sQuery(id+"F0.wireOp",EDGE,"E10.2.11"),sQuery(id+"F0.wireOp",EDGE,"E17.0"),sQuery(id+"F0.wireOp",EDGE,"E17.1"),sQuery(id+"F0.wireOp",EDGE,"E17.2"),sQuery(id+"F0.wireOp",EDGE,"E17.3"),sQuery(id+"F0.wireOp",EDGE,"E17.4"),sQuery(id+"F0.wireOp",EDGE,"E17.5"),sQuery(id+"F0.wireOp",EDGE,"E18.1.1"),sQuery(id+"F0.wireOp",EDGE,"E18.1.2"),sQuery(id+"F0.wireOp",EDGE,"E18.1.3"),sQuery(id+"F0.wireOp",EDGE,"E18.1.4"),sQuery(id+"F0.wireOp",EDGE,"E18.1.5"),sQuery(id+"F0.wireOp",EDGE,"E18.1.6"),sQuery(id+"F0.wireOp",EDGE,"E18.2.1"),sQuery(id+"F0.wireOp",EDGE,"E18.2.2"),sQuery(id+"F0.wireOp",EDGE,"E18.2.3"),sQuery(id+"F0.wireOp",EDGE,"E18.2.4"),sQuery(id+"F0.wireOp",EDGE,"E18.2.5"),sQuery(id+"F0.wireOp",EDGE,"E18.2.6")])],"isStart":false});
            var sketch = newSketch(context, id + "F8", { "sketchPlane" : qUnion([Q0])});
            skText(sketch, "E20", { "text": "STERLING", "fontName": "AllertaStencil-Regular.ttf"});
            const initialGuessF8  = {"E20": [0.01557, -0.00118, -0.53087, -0.84745, 0.003]};
            skSetInitialGuess(sketch, initialGuessF8);
            skSolve(sketch);
        }
        {
            var Q0;
            Q0 = qSketchRegion(id + "F8", true);
            extrude(context, id + "F9", {"entities" : qUnion([Q0]), "operationType" : NewBodyOperationType.REMOVE, "oppositeDirection" : true, "depth" : 0.2 * mm, "offsetDistance" : 25 * mm});
        }
    });
